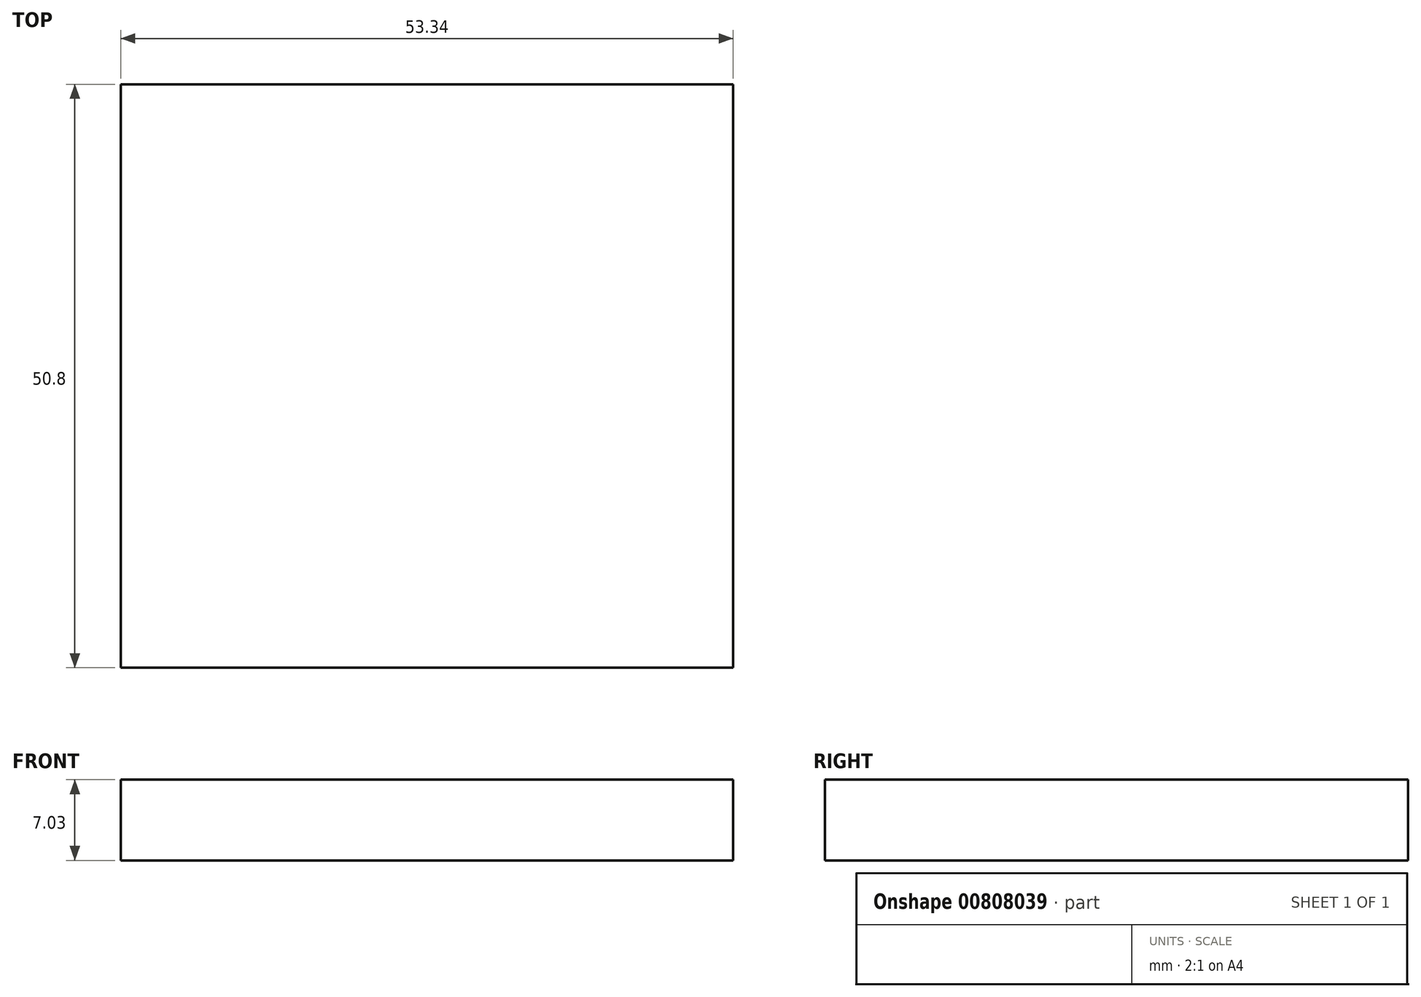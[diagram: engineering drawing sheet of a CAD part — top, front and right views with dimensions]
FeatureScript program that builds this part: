
annotation { "Feature Type Name" : "Feature", "Feature Type Description" : "" }
export const myFeature = defineFeature(function(context is Context, id is Id, definition is map)
    precondition{}
    {
        {
            var Q0;
            Q0=qCreatedBy(makeId("Front.planeOp"),FACE);
            var sketch = newSketch(context, id + "F0", { "sketchPlane" : qUnion([Q0])});
            skLineSegment(sketch, "E0.bottom", {"start": v(-44.94, 7.03) * mm, "end": v(8.4, 7.03) * mm});
            skLineSegment(sketch, "E0.top", {"start": v(-44.94, 0) * mm, "end": v(8.4, 0) * mm});
            skLineSegment(sketch, "E0.left", {"start": v(-44.94, 7.03) * mm, "end": v(-44.94, 0) * mm});
            skLineSegment(sketch, "E0.right", {"start": v(8.4, 7.03) * mm, "end": v(8.4, 0) * mm});
            skFitSpline(sketch, "E1", {"points": [v(-44.94, 7.03) * mm, v(-44.94, 44.94) * mm, v(-51.58, 69.95) * mm], "startDerivative": vector(4.02, 73.04) * mm, "endDerivative": vector(-18, 52.13) * mm});
            skFitSpline(sketch, "E2.0", {"points": [v(-39.61, 6.74) * mm, v(-39.45, 9.78) * mm, v(-39.11, 15.9) * mm, v(-38.76, 25.01) * mm, v(-38.73, 32.45) * mm, v(-38.95, 38.24) * mm, v(-39.22, 41.78) * mm, v(-39.5, 44.56) * mm, v(-39.87, 47.3) * mm, v(-40.42, 50.62) * mm, v(-41.24, 54.43) * mm, v(-42.49, 59.32) * mm, v(-44.27, 65.12) * mm, v(-45.8, 69.52) * mm, v(-46.54, 71.7) * mm]});
            skLineSegment(sketch, "E3", {"start": v(-51.58, 69.95) * mm, "end": v(-46.54, 71.7) * mm});
            skLineSegment(sketch, "E4", {"start": v(-38.77, 31.25) * mm, "end": v(-9.77, 31.25) * mm});
            skLineSegment(sketch, "E5", {"start": v(-38.76, 28.66) * mm, "end": v(-12.46, 28.66) * mm});
            skCircle(sketch, "E6", {"center": v(-10.07, 28.87) * mm, "radius": 2.4 * mm});
            skPoint(sketch, "E6.third.point", {"position": v(-7.84, 29.76) * mm});
            skLineSegment(sketch, "E7", {"start": v(-15.4, 28.66) * mm, "end": v(-15.4, 16.27) * mm});
            skLineSegment(sketch, "E8.0", {"start": v(-13.63, 28.66) * mm, "end": v(-13.63, 16.27) * mm});
            skArc(sketch, "E9", {"start": v(-24.27, 7.03) * mm, "mid": v(-17.98, 9.87) * mm, "end": v(-15.4, 16.27) * mm});
            skPoint(sketch, "E9.startSnap0", {"position": v(-24.27, 31.25) * mm});
            skArc(sketch, "E10.MirrorCS", {"start": v(-4.77, 7.03) * mm, "mid": v(-11.06, 9.87) * mm, "end": v(-13.63, 16.27) * mm});
            skSolve(sketch);
        }
        {
            var Q0;
            Q0=makeQuery(id+"F0.imprint","IMPRINT",FACE,{"disambiguationData":[TD([[makeQuery(id+"F0.imprint","IMPRINT",EDGE,{"derivedFrom":sQuery(id+"F0.wireOp",EDGE,"E0.top")}),1.0]])]});
            extrude(context, id + "F1", {"entities" : qUnion([Q0]), "depth" : 50.8 * mm, "offsetDistance" : 25.4 * mm});
        }
    });
